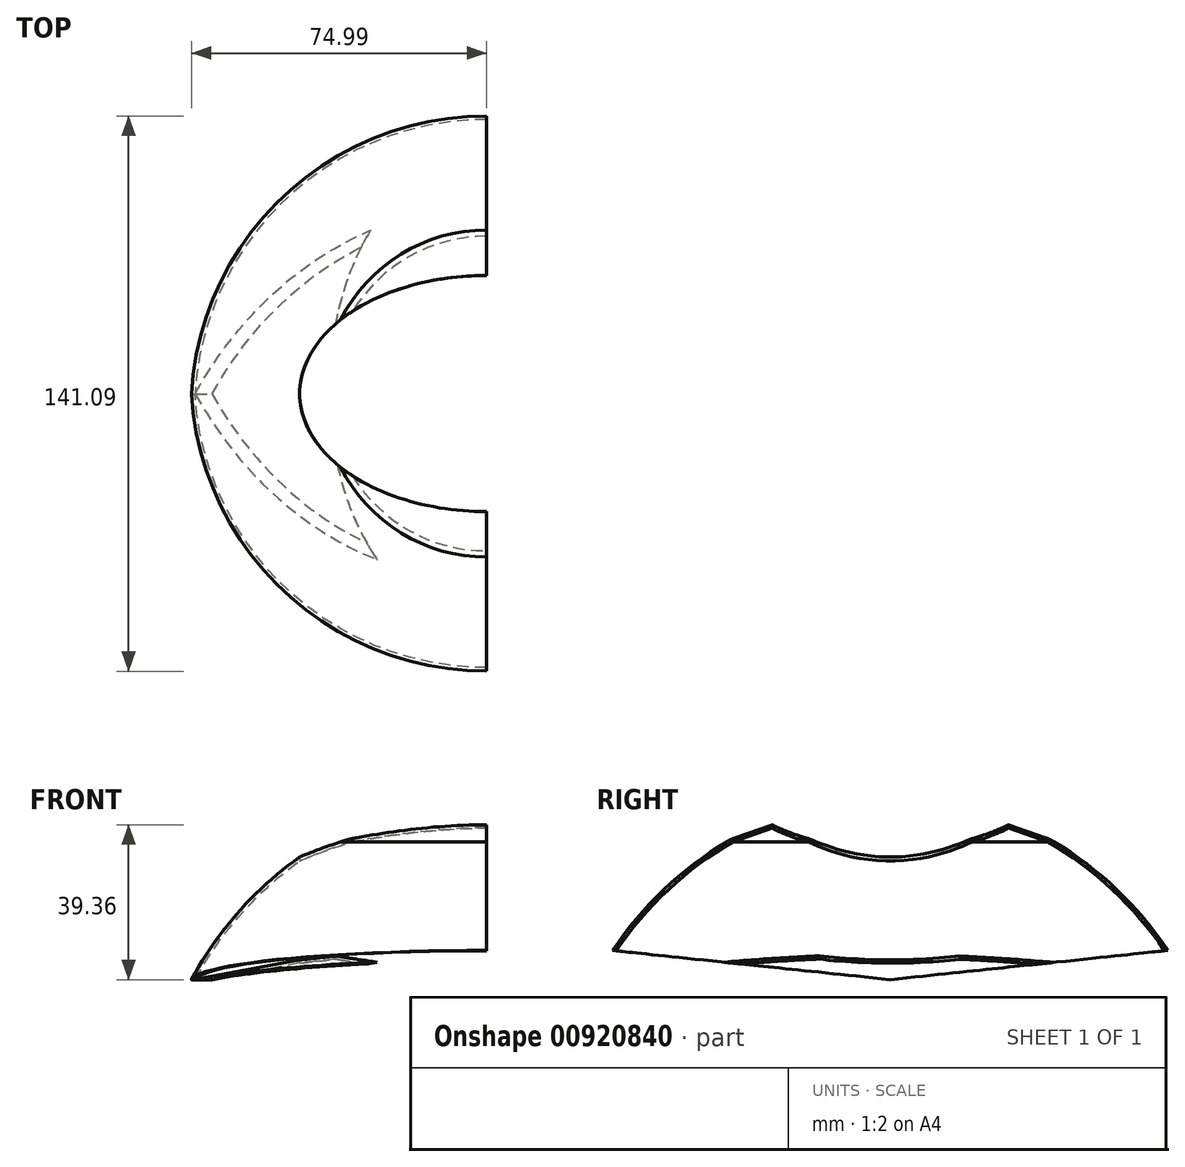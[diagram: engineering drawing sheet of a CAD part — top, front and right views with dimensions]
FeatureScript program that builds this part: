
annotation { "Feature Type Name" : "Feature", "Feature Type Description" : "" }
export const myFeature = defineFeature(function(context is Context, id is Id, definition is map)
    precondition{}
    {
        {
            var Q0;
            Q0=qCreatedBy(makeId("Right.planeOp"),FACE);
            var sketch = newSketch(context, id + "F0", { "sketchPlane" : qUnion([Q0])});
            skArc(sketch, "E0", {"start": v(-25.9, 35) * mm, "mid": v(-45.37, 19.86) * mm, "end": v(-60, 0) * mm});
            skLineSegment(sketch, "E1", {"start": v(13.28, 48.8) * mm, "end": v(13.28, 20.1) * mm});
            skPoint(sketch, "E2.orphan", {"position": v(13.28, 0) * mm});
            skArc(sketch, "E3.1", {"start": v(-27.47, 35) * mm, "mid": v(-47, 19.32) * mm, "end": v(-61.49, -1.1) * mm});
            skLineSegment(sketch, "E3.3", {"start": v(14.08, 49.6) * mm, "end": v(14.08, 19.02) * mm});
            skLineSegment(sketch, "E4", {"start": v(0, 35) * mm, "end": v(-25.9, 35) * mm});
            skLineSegment(sketch, "E5", {"start": v(-25.9, 35) * mm, "end": v(-27.47, 35) * mm});
            skLineSegment(sketch, "E6", {"start": v(-25.9, 35) * mm, "end": v(13.28, 48.8) * mm});
            skLineSegment(sketch, "E7.0", {"start": v(-25.37, 36.03) * mm, "end": v(13.02, 49.56) * mm});
            skArc(sketch, "E8", {"start": v(-25.37, 36.03) * mm, "mid": v(-26.45, 35.58) * mm, "end": v(-27.47, 35) * mm});
            skLineSegment(sketch, "E9", {"start": v(13.02, 49.56) * mm, "end": v(14.08, 49.6) * mm});
            skPoint(sketch, "E10.orphan", {"position": v(13.28, 13.8) * mm});
            skLineSegment(sketch, "E11", {"start": v(-60, 0) * mm, "end": v(13.28, 13.8) * mm});
            skLineSegment(sketch, "E12", {"start": v(14.08, 19.02) * mm, "end": v(14.08, 13.8) * mm});
            skLineSegment(sketch, "E13", {"start": v(13.28, 20.1) * mm, "end": v(13.28, 13.8) * mm});
            skLineSegment(sketch, "E14", {"start": v(14.08, 13.8) * mm, "end": v(14.08, 13.14) * mm});
            skLineSegment(sketch, "E15.0", {"start": v(-59.85, -0.79) * mm, "end": v(13.43, 13.02) * mm});
            skLineSegment(sketch, "E16", {"start": v(13.43, 13.02) * mm, "end": v(14.08, 13.14) * mm});
            skLineSegment(sketch, "E17", {"start": v(-59.85, -0.79) * mm, "end": v(-61.49, -1.1) * mm});
            skPoint(sketch, "E18.start.orphan", {"position": v(13.28, 19.02) * mm});
            skPoint(sketch, "E19.orphan", {"position": v(14.08, 13.14) * mm});
            skLineSegment(sketch, "E20", {"start": v(0.08, 0.34) * mm, "end": v(14.08, 0.34) * mm});
            skLineSegment(sketch, "E21", {"start": v(14.08, 0.34) * mm, "end": v(14.08, 13.14) * mm});
            skLineSegment(sketch, "E22.MirrorCS", {"start": v(14.08, 0.34) * mm, "end": v(-56.25, 7.73) * mm});
            skLineSegment(sketch, "E23.MirrorCS", {"start": v(14.08, 0.34) * mm, "end": v(-53.88, 0.34) * mm});
            skLineSegment(sketch, "E24", {"start": v(14.08, 0.34) * mm, "end": v(14.08, -1.25) * mm});
            skLineSegment(sketch, "E25.0", {"start": v(14, -0.46) * mm, "end": v(-56.75, 6.98) * mm});
            skPoint(sketch, "E26.orphan", {"position": v(-57.95, 7.9) * mm});
            skPoint(sketch, "E27.MirrorCS.end.orphan", {"position": v(-66.3, 0.34) * mm});
            skPoint(sketch, "E28.MirrorCS.end.orphan", {"position": v(-66.57, -1.25) * mm});
            skPoint(sketch, "E28.MirrorCS.start.orphan", {"position": v(14.08, -1.25) * mm});
            skPoint(sketch, "E29.start.orphan", {"position": v(86.1, 7.9) * mm});
            skPoint(sketch, "E30.end.orphan", {"position": v(94.46, 0.34) * mm});
            skPoint(sketch, "E30.start.orphan", {"position": v(94.73, -1.25) * mm});
            skSolve(sketch);
        }
        {
            var Q0;
            {var subQ0=sQuery(id+"F0.wireOp",EDGE,"E5");Q0=makeQuery(id+"F0.imprint","IMPRINT",FACE,{"disambiguationData":[TD([[makeQuery(id+"F0.imprint","IMPRINT",EDGE,{"derivedFrom":subQ0}),1.0]])]});}
            var Q1;
            Q1=makeQuery(id+"F0.imprint","IMPRINT",FACE,{"disambiguationData":[TD([[makeQuery(id+"F0.imprint","IMPRINT",EDGE,{"derivedFrom":sQuery(id+"F0.wireOp",EDGE,"E1")}),1.0]])]});
            var Q2;
            {var subQ0=sQuery(id+"F0.wireOp",EDGE,"E17");Q2=makeQuery(id+"F0.imprint","IMPRINT",FACE,{"disambiguationData":[TD([[makeQuery(id+"F0.imprint","IMPRINT",EDGE,{"derivedFrom":subQ0}),-1.0]])]});}
            var Q3;
            {var subQ0=sQuery(id+"F0.wireOp",EDGE,"E22.MirrorCS");var subQ1=sQuery(id+"F0.wireOp",EDGE,"E0");var subQ2=makeQuery(id+"F0.imprint","INTERSECT",VERTEX,{"derivedFrom":[subQ1,subQ0]});Q3=makeQuery(id+"F0.imprint","IMPRINT",FACE,{"disambiguationData":[TD([[makeQuery(id+"F0.imprint","IMPRINT",EDGE,{"disambiguationData":[TD([[subQ2,-1.0]])],"derivedFrom":subQ1}),-1.0]])]});}
            var Q4;
            {var subQ0=sQuery(id+"F0.wireOp",EDGE,"E25.0");var subQ1=sQuery(id+"F0.wireOp",EDGE,"E11");var subQ2=makeQuery(id+"F0.imprint","INTERSECT",VERTEX,{"derivedFrom":[subQ1,subQ0]});Q4=makeQuery(id+"F0.imprint","IMPRINT",FACE,{"disambiguationData":[TD([[makeQuery(id+"F0.imprint","IMPRINT",EDGE,{"disambiguationData":[TD([[subQ2,-1.0]])],"derivedFrom":subQ1}),-1.0]])]});}
            var Q5;
            Q5=sQuery(id+"F0.wireOp",EDGE,"E3.3");
            revolve(context, id + "F1", {"surfaceOperationType" : NewSurfaceOperationType.NEW, "entities" : qUnion([Q0, Q1, Q2, Q3, Q4]), "axis" : qUnion([Q5]), "revolveType" : RevolveType.ONE_DIRECTION, "angle" : 180 * degree});
        }
        {
            var Q0;
            Q0=qCreatedBy(makeId("Top.planeOp"),FACE);
            var sketch = newSketch(context, id + "F2", { "sketchPlane" : qUnion([Q0])});
            skLineSegment(sketch, "E31", {"start": v(0, 0) * mm, "end": v(0, 15) * mm});
            skEllipse(sketch, "E32", {"center": v(0, 15) * mm, "majorRadius": 60 * mm, "minorRadius": 40 * mm, "majorAxis": v(0, 1)});
            skLineSegment(sketch, "E33", {"start": v(0, 15) * mm, "end": v(-77.56, 15) * mm});
            skLineSegment(sketch, "E34", {"start": v(0, 15) * mm, "end": v(0, 15.8) * mm});
            skLineSegment(sketch, "E35", {"start": v(0, 15.8) * mm, "end": v(-77.56, 15.8) * mm});
            skLineSegment(sketch, "E36", {"start": v(-77.56, 15.8) * mm, "end": v(-77.56, 15) * mm});
            skSolve(sketch);
        }
        {
            var Q0;
            {var subQ5=sQuery(id+"F2.wireOp",EDGE,"E34");Q0=makeQuery(id+"F2.imprint","IMPRINT",FACE,{"disambiguationData":[TD([[makeQuery(id+"F2.imprint","IMPRINT",EDGE,{"derivedFrom":subQ5}),-1.0]])]});}
            var Q1;
            {var subQ5=sQuery(id+"F2.wireOp",EDGE,"E34");Q1=makeQuery(id+"F2.imprint","IMPRINT",FACE,{"disambiguationData":[TD([[makeQuery(id+"F2.imprint","IMPRINT",EDGE,{"derivedFrom":subQ5}),1.0]])]});}
            extrude(context, id + "F3", {"entities" : qUnion([Q0, Q1]), "operationType" : NewBodyOperationType.REMOVE, "depth" : 16 * mm, "offsetDistance" : 25 * mm});
        }
        {
            var Q0;
            Q0 = qSketchRegion(id + "FCvOXFBJb9eC6t3_1", true);
            var Q1;
            {var subQ5=sQuery(id+"F2.wireOp",EDGE,"E34");Q1=makeQuery(id+"F2.imprint","IMPRINT",FACE,{"disambiguationData":[TD([[makeQuery(id+"F2.imprint","IMPRINT",EDGE,{"derivedFrom":subQ5}),-1.0]])]});}
            extrude(context, id + "F4", {"entities" : qUnion([Q0, Q1]), "operationType" : NewBodyOperationType.REMOVE, "depth" : 10 * mm, "offsetDistance" : 25 * mm});
        }
        {
            var Q0;
            Q0=qCreatedBy(makeId("Top.planeOp"),FACE);
            var sketch = newSketch(context, id + "F5", { "sketchPlane" : qUnion([Q0])});
            skPoint(sketch, "E37", {"position": v(0, 14.08) * mm});
            skEllipse(sketch, "E38", {"center": v(0, 14.08) * mm, "majorRadius": 47.5 * mm, "minorRadius": 30 * mm, "majorAxis": v(-1, 0)});
            skSolve(sketch);
        }
        {
            var Q0;
            Q0=makeQuery(id+"F5.imprint","IMPRINT",FACE,{"disambiguationData":[TD([[makeQuery(id+"F5.imprint","IMPRINT",EDGE,{"derivedFrom":sQuery(id+"F5.wireOp",EDGE,"E38")}),1.0]])]});
            extrude(context, id + "F6", {"entities" : qUnion([Q0]), "operationType" : NewBodyOperationType.REMOVE, "depth" : 100 * mm, "offsetDistance" : 25 * mm});
        }
        {
            var Q0;
            Q0=qCreatedBy(makeId("Right.planeOp"),FACE);
            var sketch = newSketch(context, id + "F7", { "sketchPlane" : qUnion([Q0])});
            skLineSegment(sketch, "E39", {"start": v(0, 0) * mm, "end": v(14, 0) * mm});
            skLineSegment(sketch, "E40", {"start": v(14, 0) * mm, "end": v(14, 12.8) * mm});
            skLineSegment(sketch, "E41", {"start": v(14, 0) * mm, "end": v(94.42, 0) * mm});
            skLineSegment(sketch, "E42", {"start": v(14, 0) * mm, "end": v(86.03, 7.57) * mm});
            skLineSegment(sketch, "E43", {"start": v(86.03, 7.57) * mm, "end": v(94.42, 0) * mm});
            skLineSegment(sketch, "E44.MirrorCS", {"start": v(14, 0) * mm, "end": v(-58.03, 7.57) * mm});
            skLineSegment(sketch, "E45.MirrorCS", {"start": v(14, 0) * mm, "end": v(-66.42, 0) * mm});
            skLineSegment(sketch, "E46.MirrorCS", {"start": v(-58.03, 7.57) * mm, "end": v(-66.42, 0) * mm});
            skLineSegment(sketch, "E47", {"start": v(14, 0) * mm, "end": v(14, -1.59) * mm});
            skLineSegment(sketch, "E48", {"start": v(14, -1.59) * mm, "end": v(94.7, -1.59) * mm});
            skLineSegment(sketch, "E49", {"start": v(94.7, -1.59) * mm, "end": v(94.42, 0) * mm});
            skLineSegment(sketch, "E50.MirrorCS", {"start": v(14, -1.59) * mm, "end": v(-66.7, -1.59) * mm});
            skLineSegment(sketch, "E51.MirrorCS", {"start": v(-66.7, -1.59) * mm, "end": v(-66.42, 0) * mm});
            skSolve(sketch);
        }
        {
            var Q0;
            {var subQ2=makeQuery(id+"F7.imprint","IMPRINT",EDGE,{"derivedFrom":sQuery(id+"F7.wireOp",EDGE,"E39")});var subQ3=makeQuery(id+"F7.imprint","IMPRINT",EDGE,{"derivedFrom":sQuery(id+"F7.wireOp",EDGE,"E41")});Q0=qUnion([makeQuery(id+"F7.imprint","IMPRINT",FACE,{"disambiguationData":[TD([[subQ3,-1.0]])]}),makeQuery(id+"F7.imprint","IMPRINT",FACE,{"disambiguationData":[TD([[subQ2,1.0]])]}),makeQuery(id+"F7.imprint","IMPRINT",FACE,{"disambiguationData":[TD([[subQ3,1.0]])]}),makeQuery(id+"F7.imprint","IMPRINT",FACE,{"disambiguationData":[TD([[subQ2,-1.0]])]})]);}
            extrude(context, id + "F8", {"entities" : qUnion([Q0]), "operationType" : NewBodyOperationType.REMOVE, "oppositeDirection" : true, "depth" : 120 * mm, "offsetDistance" : 25 * mm});
        }
    });
